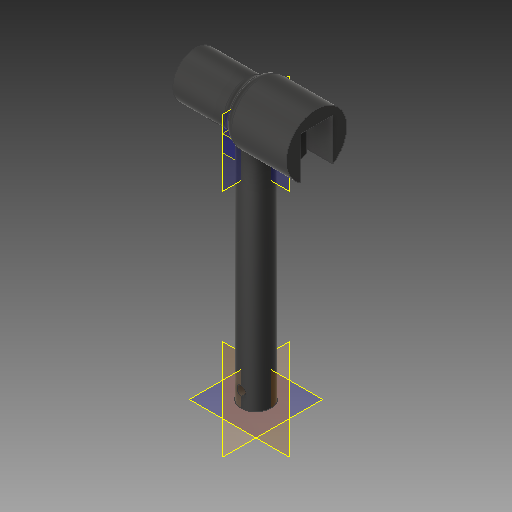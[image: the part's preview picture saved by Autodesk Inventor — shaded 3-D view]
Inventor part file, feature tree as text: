
AUTODESK INVENTOR PART (.ipt)
format: ipt  version: 2018 (Build 220112000, 112)  size: 365,568 bytes
history: native  units: mm
features: extrude x14, sketch x13, plane x6, fillet x3, other x1
ambient origin geometry x8: Origin, YZ Plane, XZ Plane, XY Plane, X Axis, Y Axis, Z Axis, Center Point
bodies: Body1 (feature_tree)
feature tree (37):
  other  "Sólido1"
  extrude  "Extrusión1"  Depth=10.0mm TaperAngle=0.0deg
  plane  "Plano de trabajo1"
  plane  "Plano de trabajo2"
  plane  "Plano de trabajo3"
  extrude  "Extrusión2"  Depth=20.0mm TaperAngle=0.0deg
  extrude  "Extrusión3"  Depth=20.0mm TaperAngle=0.0deg
  fillet  "Empalme1"  Radius=3.0mm
  extrude  "Extrusión4"  Depth=2.0mm
  sketch  "Boceto7"  dims[d14=2.0mm d15=2.0mm]
  sketch  "Boceto8"  dims[d16=2.9mm d17=2.0mm]
  extrude  "Extrusión8"  Depth=2.0mm
  extrude  "Extrusion12"  Depth=7.9mm TaperAngle=0.0deg
  extrude  "Extrusion13"  Depth=10.0mm TaperAngle=0.0deg
  sketch  "Sketch13"  dims[d32=14.8mm d33=20.0mm d34=0.0mm d47=10.0mm]
  fillet  "Fillet4"  Radius=10.0mm
  extrude  "Extrusion15"  Depth=10.0mm
  extrude  "Extrusion16"  Depth=10.0mm
  extrude  "Extrusion17"  Depth=10.0mm
  extrude  "Extrusion18"  Depth=0.5mm
  extrude  "Extrusion19"  Depth=7.9mm TaperAngle=0.0deg
  fillet  "Fillet6"  Radius=5.9mm
  plane  "Work Plane4"
  plane  "Work Plane5"
  extrude  "Extrusion20"  Depth=10.0mm
  plane  "Work Plane6"
  extrude  "Extrusion21"  Depth=5.0mm TaperAngle=0.0deg
  sketch  "Boceto1"  dims[d0=10.0mm d1=78.0mm d2=0.0mm]
  sketch  "Boceto3"  dims[d6=20.0mm d7=20.0mm d8=0.0mm]
  sketch  "Boceto4"  dims[d9=15.0mm d10=20.0mm d11=0.0mm d12=3.0mm]
  sketch  "Boceto9"  dims[d18=2.9mm d19=7.9mm d20=0.0mm]
  sketch  "Sketch14"  dims[d48=10.0mm d49=0.0mm d50=5.5mm]
  sketch  "Sketch15"  dims[d51=5.0mm d52=10.0mm]
  sketch  "Sketch16"  dims[d53=10.0mm d54=0.0mm d59=3.0mm]
  sketch  "Sketch17"  dims[d60=7.9mm d61=0.0mm d62=0.5mm]
  sketch  "Sketch19"  dims[d63=0.5mm d64=7.9mm d65=0.0mm d66=5.9mm]
  sketch  "Sketch22"  dims[d67=0.8mm d68=0.8mm d69=5.0mm d70=0.0mm d71=15.0mm d72=20.0mm d73=0.0mm d74=4.0mm d75=0.0mm d77=2.0mm d79=5.0mm d80=3.0mm d81=10.0mm d82=0.0mm d90=3.0mm d91=2.0mm d92=6.0mm d93=4.0mm d94=10.0mm d95=0.0mm]
